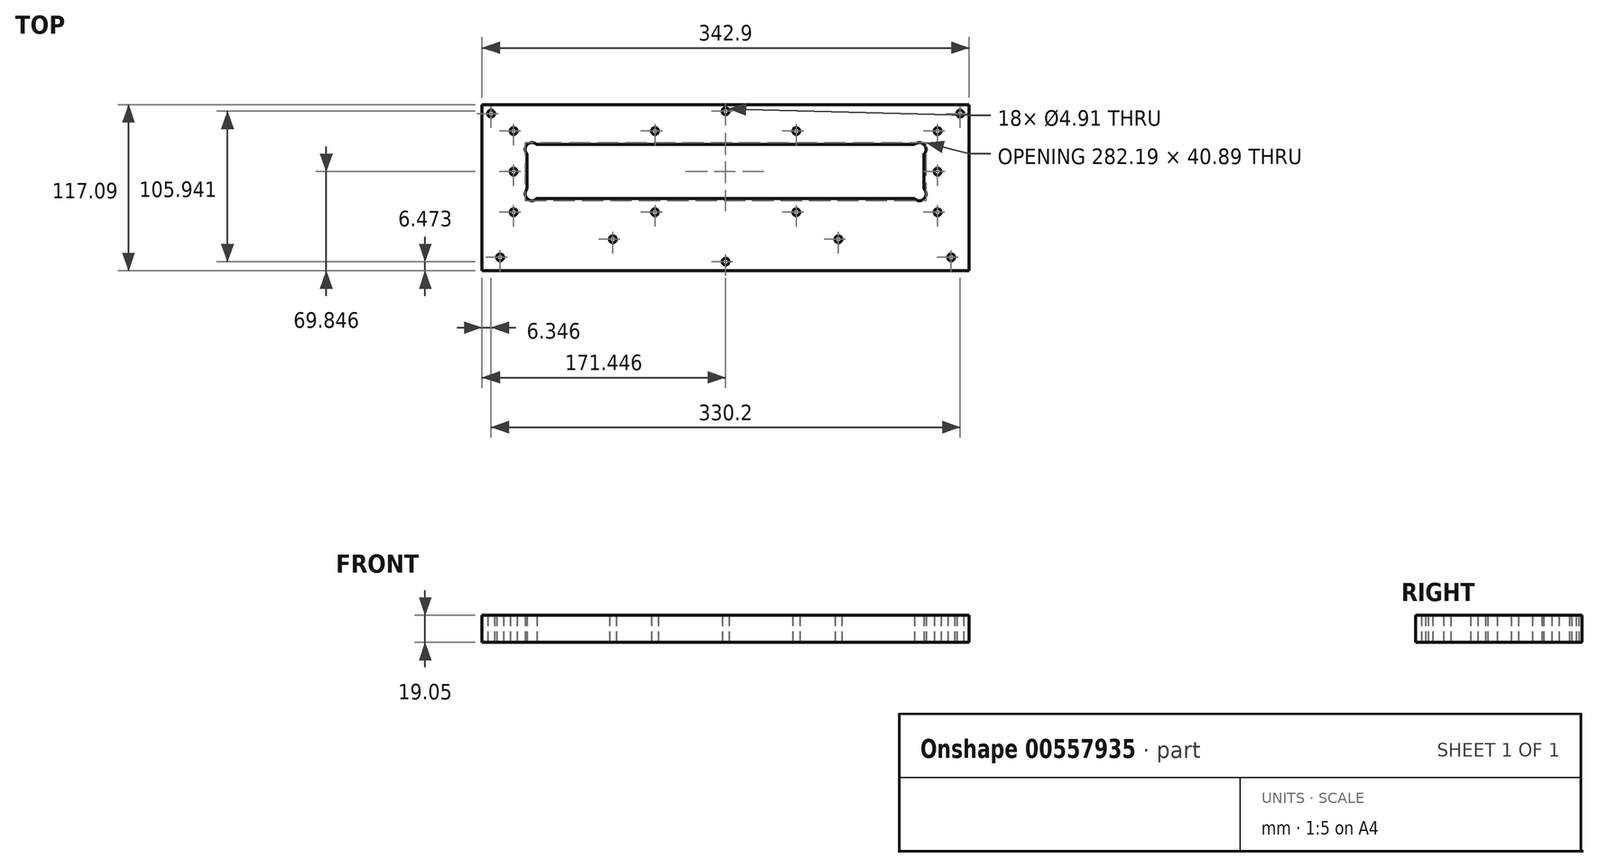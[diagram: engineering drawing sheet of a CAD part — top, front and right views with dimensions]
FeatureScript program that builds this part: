
annotation { "Feature Type Name" : "Feature", "Feature Type Description" : "" }
export const myFeature = defineFeature(function(context is Context, id is Id, definition is map)
    precondition{}
    {
        {
            var Q0;
            Q0=qCreatedBy(makeId("Top.planeOp"),FACE);
            var sketch = newSketch(context, id + "F0", { "sketchPlane" : qUnion([Q0])});
            skLineSegment(sketch, "E0", {"start": v(59.72, 92.85) * mm, "end": v(59.72, 117.48) * mm});
            skLineSegment(sketch, "E1", {"start": v(66.45, 124.22) * mm, "end": v(332.38, 124.22) * mm});
            skLineSegment(sketch, "E2", {"start": v(339.12, 92.85) * mm, "end": v(339.12, 117.48) * mm});
            skLineSegment(sketch, "E3", {"start": v(66.45, 86.12) * mm, "end": v(332.38, 86.12) * mm});
            skCircle(sketch, "E4", {"center": v(149.67, 133.74) * mm, "radius": 2.46 * mm});
            skCircle(sketch, "E5", {"center": v(249.16, 133.74) * mm, "radius": 2.46 * mm});
            skCircle(sketch, "E6", {"center": v(50.2, 105.17) * mm, "radius": 2.46 * mm});
            skCircle(sketch, "E7", {"center": v(348.64, 105.17) * mm, "radius": 2.46 * mm});
            skCircle(sketch, "E8", {"center": v(50.2, 133.74) * mm, "radius": 2.46 * mm});
            skCircle(sketch, "E9", {"center": v(348.64, 133.74) * mm, "radius": 2.46 * mm});
            skCircle(sketch, "E10", {"center": v(149.67, 76.6) * mm, "radius": 2.46 * mm});
            skCircle(sketch, "E11", {"center": v(249.16, 76.6) * mm, "radius": 2.46 * mm});
            skCircle(sketch, "E12", {"center": v(50.2, 76.6) * mm, "radius": 2.46 * mm});
            skCircle(sketch, "E13", {"center": v(348.64, 76.6) * mm, "radius": 2.46 * mm});
            skCircle(sketch, "E14", {"center": v(199.42, 41.8) * mm, "radius": 2.46 * mm});
            skCircle(sketch, "E15", {"center": v(34.32, 146.06) * mm, "radius": 2.46 * mm});
            skCircle(sketch, "E16", {"center": v(364.52, 146.06) * mm, "radius": 2.46 * mm});
            skCircle(sketch, "E17", {"center": v(40.67, 44.84) * mm, "radius": 2.46 * mm});
            skCircle(sketch, "E18", {"center": v(358.17, 44.84) * mm, "radius": 2.46 * mm});
            skCircle(sketch, "E19", {"center": v(199.42, 147.73) * mm, "radius": 2.46 * mm});
            skCircle(sketch, "E20", {"center": v(278.8, 57.6) * mm, "radius": 2.46 * mm});
            skCircle(sketch, "E21.MirrorC", {"center": v(120.04, 57.6) * mm, "radius": 2.46 * mm});
            skArc(sketch, "E22", {"start": v(59.72, 92.85) * mm, "mid": v(59.72, 86.12) * mm, "end": v(66.45, 86.12) * mm});
            skArc(sketch, "E23", {"start": v(339.12, 117.48) * mm, "mid": v(339.12, 124.22) * mm, "end": v(332.38, 124.22) * mm});
            skArc(sketch, "E24.trimOffspring", {"start": v(332.38, 86.12) * mm, "mid": v(339.12, 86.12) * mm, "end": v(339.12, 92.85) * mm});
            skArc(sketch, "E25.trimOffspring", {"start": v(66.45, 124.22) * mm, "mid": v(59.72, 124.22) * mm, "end": v(59.72, 117.48) * mm});
            skLineSegment(sketch, "E26.bottom", {"start": v(27.97, 35.32) * mm, "end": v(370.87, 35.32) * mm});
            skLineSegment(sketch, "E26.top", {"start": v(27.97, 152.41) * mm, "end": v(370.87, 152.41) * mm});
            skLineSegment(sketch, "E26.left", {"start": v(27.97, 35.32) * mm, "end": v(27.97, 152.41) * mm});
            skLineSegment(sketch, "E26.right", {"start": v(370.87, 35.32) * mm, "end": v(370.87, 152.41) * mm});
            skSolve(sketch);
        }
        {
            var Q0;
            Q0=makeQuery(id+"F0.imprint","IMPRINT",FACE,{"disambiguationData":[TD([[makeQuery(id+"F0.imprint","IMPRINT",EDGE,{"derivedFrom":sQuery(id+"F0.wireOp",EDGE,"E0")}),1.0]])]});
            extrude(context, id + "F1", {"entities" : qUnion([Q0]), "depth" : 19.05 * mm, "offsetDistance" : 25 * mm});
        }
    });
